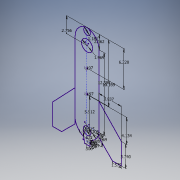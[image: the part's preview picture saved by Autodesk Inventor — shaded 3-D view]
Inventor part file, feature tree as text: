
AUTODESK INVENTOR PART (.ipt)
format: ipt  version: 2016 (Build 200138000, 138)  size: 119,296 bytes
history: native  units: in
note: dims shown in document units (in); Inventor stores cm internally (conversion verified against a paired STEP export)
features: sketch x1
ambient origin geometry x8: Origin, YZ Plane, XZ Plane, XY Plane, X Axis, Y Axis, Z Axis, Center Point
feature tree (1):
  sketch  "Sketch1"  dims[d8=2.5152in d16=0.436in d17=0.5059in d18=0.1201in d19=0.3926in d20=0.7323in d21=0.4094in d22=0.622in d23=2.1063in d24=1.9685in d25=12.5984in d27=2.3622in d28=5.5118in d29=3.937in d30=4.1339in d31=3.7402in d32=1.5748in d34=0.7874in d35=1.1811in d36=1.9685in d37=2.7559in d38=1.1811in d39=1.378in d40=10.1693in d41=6.2205in d42=0.1969in d43=0.1969in]
